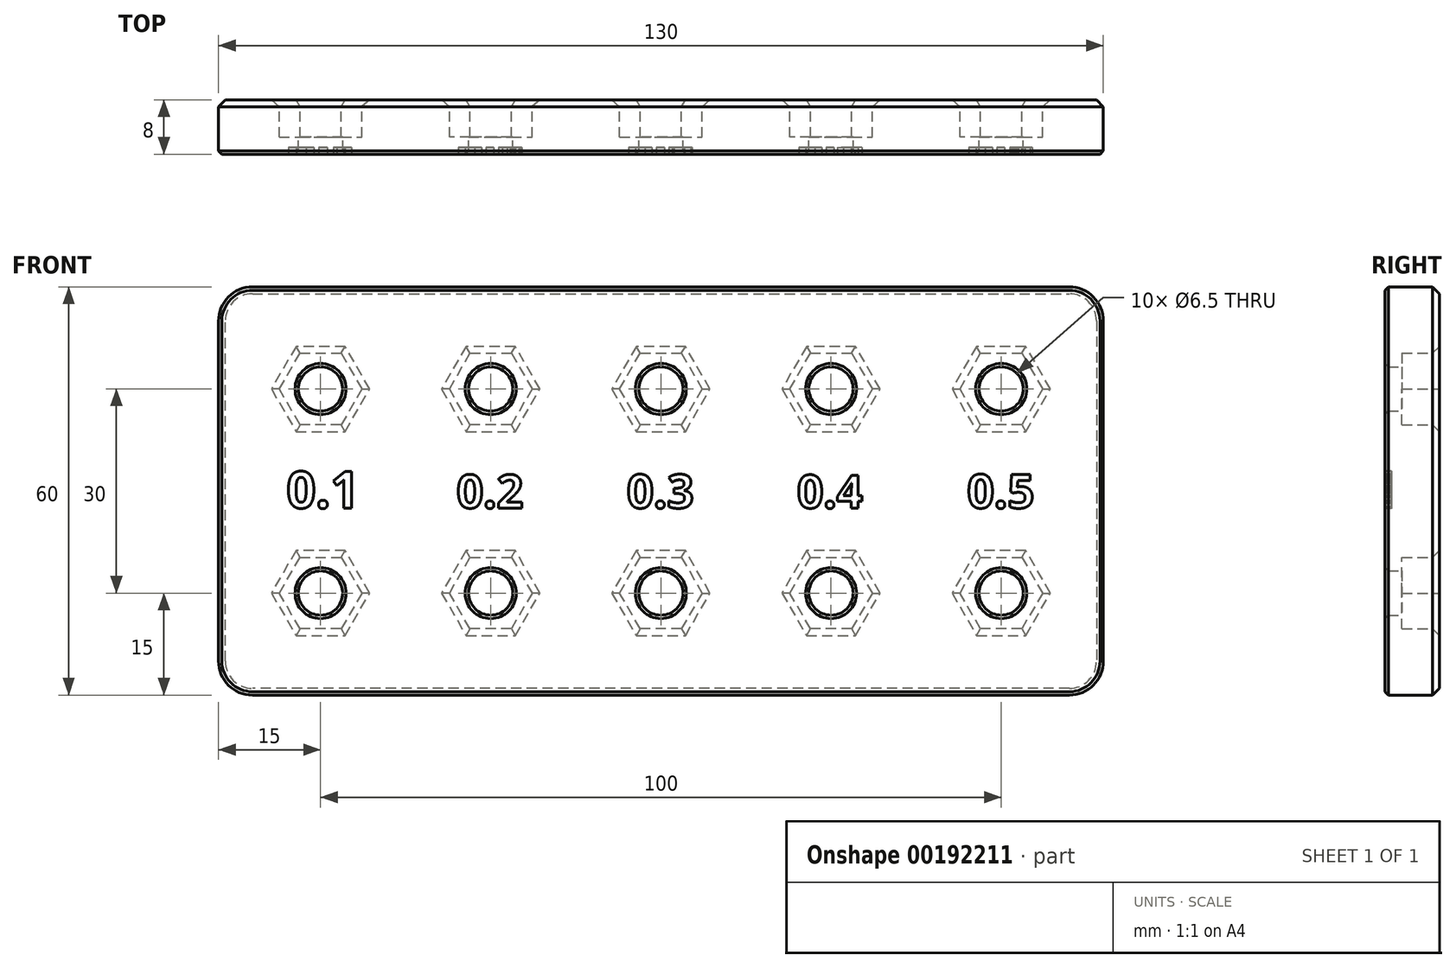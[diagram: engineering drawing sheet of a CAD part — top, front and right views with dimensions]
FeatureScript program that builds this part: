
annotation { "Feature Type Name" : "Feature", "Feature Type Description" : "" }
export const myFeature = defineFeature(function(context is Context, id is Id, definition is map)
    precondition{}
    {
        {
            var Q0;
            Q0=qCreatedBy(makeId("Front.planeOp"),FACE);
            var sketch = newSketch(context, id + "F0", { "sketchPlane" : qUnion([Q0])});
            skLineSegment(sketch, "E0.bottom", {"start": v(5, 0) * mm, "end": v(125, 0) * mm});
            skLineSegment(sketch, "E0.top", {"start": v(5, 60) * mm, "end": v(125, 60) * mm});
            skLineSegment(sketch, "E0.left", {"start": v(0, 5) * mm, "end": v(0, 55) * mm});
            skLineSegment(sketch, "E0.right", {"start": v(130, 5) * mm, "end": v(130, 55) * mm});
            skPoint(sketch, "E1.visualSharp", {"position": v(0, 60) * mm});
            skArc(sketch, "E1.filletArc", {"start": v(5, 60) * mm, "mid": v(1.46, 58.54) * mm, "end": v(0, 55) * mm});
            skPoint(sketch, "E2.visualSharp", {"position": v(130, 60) * mm});
            skArc(sketch, "E2.filletArc", {"start": v(130, 55) * mm, "mid": v(128.54, 58.54) * mm, "end": v(125, 60) * mm});
            skPoint(sketch, "E3.visualSharp", {"position": v(130, 0) * mm});
            skArc(sketch, "E3.filletArc", {"start": v(125, 0) * mm, "mid": v(128.54, 1.46) * mm, "end": v(130, 5) * mm});
            skPoint(sketch, "E4.visualSharp", {"position": v(0, 0) * mm});
            skArc(sketch, "E4.filletArc", {"start": v(0, 5) * mm, "mid": v(1.46, 1.46) * mm, "end": v(5, 0) * mm});
            skLineSegment(sketch, "E5", {"start": v(0, 45) * mm, "end": v(130, 45) * mm, "construction": true});
            skLineSegment(sketch, "E6", {"start": v(0, 15) * mm, "end": v(130, 15) * mm, "construction": true});
            skLineSegment(sketch, "E7", {"start": v(15, 60) * mm, "end": v(15, 0) * mm, "construction": true});
            skLineSegment(sketch, "E8.1.0.0", {"start": v(40, 60) * mm, "end": v(40, 0) * mm, "construction": true});
            skLineSegment(sketch, "E8.2.0.0", {"start": v(65, 60) * mm, "end": v(65, 0) * mm, "construction": true});
            skLineSegment(sketch, "E8.3.0.0", {"start": v(90, 60) * mm, "end": v(90, 0) * mm, "construction": true});
            skLineSegment(sketch, "E8.4.0.0", {"start": v(115, 60) * mm, "end": v(115, 0) * mm, "construction": true});
            skLineSegment(sketch, "E8.direction1", {"start": v(15, 0) * mm, "end": v(40, 0) * mm, "construction": true});
            skCircle(sketch, "E9", {"center": v(15, 45) * mm, "radius": 3.25 * mm});
            skCircle(sketch, "E10", {"center": v(40, 45) * mm, "radius": 3.25 * mm});
            skCircle(sketch, "E11", {"center": v(65, 45) * mm, "radius": 3.25 * mm});
            skCircle(sketch, "E12", {"center": v(90, 45) * mm, "radius": 3.25 * mm});
            skCircle(sketch, "E13", {"center": v(115, 45) * mm, "radius": 3.25 * mm});
            skCircle(sketch, "E14", {"center": v(15, 15) * mm, "radius": 3.25 * mm});
            skCircle(sketch, "E15", {"center": v(40, 15) * mm, "radius": 3.25 * mm});
            skCircle(sketch, "E16", {"center": v(65, 15) * mm, "radius": 3.25 * mm});
            skCircle(sketch, "E17", {"center": v(90, 15) * mm, "radius": 3.25 * mm});
            skCircle(sketch, "E18", {"center": v(115, 15) * mm, "radius": 3.25 * mm});
            skSolve(sketch);
        }
        {
            var Q0;
            Q0=makeQuery(id+"F0.imprint","IMPRINT",FACE,{"disambiguationData":[TD([[makeQuery(id+"F0.imprint","IMPRINT",EDGE,{"derivedFrom":sQuery(id+"F0.wireOp",EDGE,"E0.bottom")}),1.0]])]});
            extrude(context, id + "F1", {"entities" : qUnion([Q0]), "depth" : 8 * mm});
        }
        {
            var Q0;
            Q0=makeQuery(id+"F1.opExtrude","CAP_FACE",FACE,{"disambiguationData":[OSD([sQuery(id+"F0.wireOp",EDGE,"E0.bottom"),sQuery(id+"F0.wireOp",EDGE,"E0.top"),sQuery(id+"F0.wireOp",EDGE,"E0.left"),sQuery(id+"F0.wireOp",EDGE,"E0.right"),sQuery(id+"F0.wireOp",EDGE,"E1.filletArc"),sQuery(id+"F0.wireOp",EDGE,"E2.filletArc"),sQuery(id+"F0.wireOp",EDGE,"E3.filletArc"),sQuery(id+"F0.wireOp",EDGE,"E4.filletArc"),sQuery(id+"F0.wireOp",EDGE,"E9"),sQuery(id+"F0.wireOp",EDGE,"E10"),sQuery(id+"F0.wireOp",EDGE,"E11"),sQuery(id+"F0.wireOp",EDGE,"E12"),sQuery(id+"F0.wireOp",EDGE,"E13"),sQuery(id+"F0.wireOp",EDGE,"E14"),sQuery(id+"F0.wireOp",EDGE,"E15"),sQuery(id+"F0.wireOp",EDGE,"E16"),sQuery(id+"F0.wireOp",EDGE,"E17"),sQuery(id+"F0.wireOp",EDGE,"E18")])],"isStart":true});
            var sketch = newSketch(context, id + "F2", { "sketchPlane" : qUnion([Q0])});
            skCircle(sketch, "E19.cCircle", {"center": v(-115, 45) * mm, "radius": 5.25 * mm, "construction": true});
            skLineSegment(sketch, "E19.0", {"start": v(-108.94, 45) * mm, "end": v(-111.97, 39.75) * mm});
            skLineSegment(sketch, "E19.1", {"start": v(-111.97, 39.75) * mm, "end": v(-118.03, 39.75) * mm});
            skLineSegment(sketch, "E19.2", {"start": v(-118.03, 39.75) * mm, "end": v(-121.06, 45) * mm});
            skLineSegment(sketch, "E19.3", {"start": v(-121.06, 45) * mm, "end": v(-118.03, 50.25) * mm});
            skLineSegment(sketch, "E19.4", {"start": v(-118.03, 50.25) * mm, "end": v(-111.97, 50.25) * mm});
            skLineSegment(sketch, "E19.5", {"start": v(-111.97, 50.25) * mm, "end": v(-108.94, 45) * mm});
            skPoint(sketch, "E19.0.midPoint", {"position": v(-110.45, 42.37) * mm});
            skLineSegment(sketch, "E20", {"start": v(-130, 30) * mm, "end": v(0, 30) * mm, "construction": true});
            skPoint(sketch, "E21.1.0.0", {"position": v(-85.45, 42.37) * mm});
            skLineSegment(sketch, "E21.1.0.1", {"start": v(-93.03, 50.25) * mm, "end": v(-86.97, 50.25) * mm});
            skCircle(sketch, "E21.1.0.2", {"center": v(-90, 45) * mm, "radius": 5.25 * mm, "construction": true});
            skLineSegment(sketch, "E21.1.0.3", {"start": v(-83.94, 45) * mm, "end": v(-86.97, 39.75) * mm});
            skLineSegment(sketch, "E21.1.0.4", {"start": v(-86.97, 39.75) * mm, "end": v(-93.03, 39.75) * mm});
            skLineSegment(sketch, "E21.1.0.5", {"start": v(-96.06, 45) * mm, "end": v(-93.03, 50.25) * mm});
            skLineSegment(sketch, "E21.1.0.6", {"start": v(-93.03, 39.75) * mm, "end": v(-96.06, 45) * mm});
            skLineSegment(sketch, "E21.1.0.7", {"start": v(-86.97, 50.25) * mm, "end": v(-83.94, 45) * mm});
            skPoint(sketch, "E21.2.0.0", {"position": v(-60.45, 42.37) * mm});
            skLineSegment(sketch, "E21.2.0.1", {"start": v(-68.03, 50.25) * mm, "end": v(-61.97, 50.25) * mm});
            skCircle(sketch, "E21.2.0.2", {"center": v(-65, 45) * mm, "radius": 5.25 * mm, "construction": true});
            skLineSegment(sketch, "E21.2.0.3", {"start": v(-58.94, 45) * mm, "end": v(-61.97, 39.75) * mm});
            skLineSegment(sketch, "E21.2.0.4", {"start": v(-61.97, 39.75) * mm, "end": v(-68.03, 39.75) * mm});
            skLineSegment(sketch, "E21.2.0.5", {"start": v(-71.06, 45) * mm, "end": v(-68.03, 50.25) * mm});
            skLineSegment(sketch, "E21.2.0.6", {"start": v(-68.03, 39.75) * mm, "end": v(-71.06, 45) * mm});
            skLineSegment(sketch, "E21.2.0.7", {"start": v(-61.97, 50.25) * mm, "end": v(-58.94, 45) * mm});
            skPoint(sketch, "E21.3.0.0", {"position": v(-35.45, 42.37) * mm});
            skLineSegment(sketch, "E21.3.0.1", {"start": v(-43.03, 50.25) * mm, "end": v(-36.97, 50.25) * mm});
            skCircle(sketch, "E21.3.0.2", {"center": v(-40, 45) * mm, "radius": 5.25 * mm, "construction": true});
            skLineSegment(sketch, "E21.3.0.3", {"start": v(-33.94, 45) * mm, "end": v(-36.97, 39.75) * mm});
            skLineSegment(sketch, "E21.3.0.4", {"start": v(-36.97, 39.75) * mm, "end": v(-43.03, 39.75) * mm});
            skLineSegment(sketch, "E21.3.0.5", {"start": v(-46.06, 45) * mm, "end": v(-43.03, 50.25) * mm});
            skLineSegment(sketch, "E21.3.0.6", {"start": v(-43.03, 39.75) * mm, "end": v(-46.06, 45) * mm});
            skLineSegment(sketch, "E21.3.0.7", {"start": v(-36.97, 50.25) * mm, "end": v(-33.94, 45) * mm});
            skPoint(sketch, "E21.4.0.0", {"position": v(-10.45, 42.37) * mm});
            skLineSegment(sketch, "E21.4.0.1", {"start": v(-18.03, 50.25) * mm, "end": v(-11.97, 50.25) * mm});
            skCircle(sketch, "E21.4.0.2", {"center": v(-15, 45) * mm, "radius": 5.25 * mm, "construction": true});
            skLineSegment(sketch, "E21.4.0.3", {"start": v(-8.94, 45) * mm, "end": v(-11.97, 39.75) * mm});
            skLineSegment(sketch, "E21.4.0.4", {"start": v(-11.97, 39.75) * mm, "end": v(-18.03, 39.75) * mm});
            skLineSegment(sketch, "E21.4.0.5", {"start": v(-21.06, 45) * mm, "end": v(-18.03, 50.25) * mm});
            skLineSegment(sketch, "E21.4.0.6", {"start": v(-18.03, 39.75) * mm, "end": v(-21.06, 45) * mm});
            skLineSegment(sketch, "E21.4.0.7", {"start": v(-11.97, 50.25) * mm, "end": v(-8.94, 45) * mm});
            skLineSegment(sketch, "E21.direction1", {"start": v(-118.03, 39.75) * mm, "end": v(-93.03, 39.75) * mm, "construction": true});
            skLineSegment(sketch, "E22.MirrorCS", {"start": v(-43.03, 20.25) * mm, "end": v(-46.06, 15) * mm});
            skLineSegment(sketch, "E23.MirrorCS", {"start": v(-18.03, 9.75) * mm, "end": v(-11.97, 9.75) * mm});
            skLineSegment(sketch, "E24.MirrorCS", {"start": v(-68.03, 20.25) * mm, "end": v(-71.06, 15) * mm});
            skLineSegment(sketch, "E25.MirrorCS", {"start": v(-46.06, 15) * mm, "end": v(-43.03, 9.75) * mm});
            skLineSegment(sketch, "E26.MirrorCS", {"start": v(-11.97, 9.75) * mm, "end": v(-8.94, 15) * mm});
            skLineSegment(sketch, "E27.MirrorCS", {"start": v(-36.97, 9.75) * mm, "end": v(-33.94, 15) * mm});
            skLineSegment(sketch, "E28.MirrorCS", {"start": v(-71.06, 15) * mm, "end": v(-68.03, 9.75) * mm});
            skLineSegment(sketch, "E29.MirrorCS", {"start": v(-61.97, 9.75) * mm, "end": v(-58.94, 15) * mm});
            skLineSegment(sketch, "E30.MirrorCS", {"start": v(-8.94, 15) * mm, "end": v(-11.97, 20.25) * mm});
            skLineSegment(sketch, "E31.MirrorCS", {"start": v(-43.03, 9.75) * mm, "end": v(-36.97, 9.75) * mm});
            skLineSegment(sketch, "E32.MirrorCS", {"start": v(-61.97, 20.25) * mm, "end": v(-68.03, 20.25) * mm});
            skLineSegment(sketch, "E33.MirrorCS", {"start": v(-18.03, 20.25) * mm, "end": v(-21.06, 15) * mm});
            skLineSegment(sketch, "E34.MirrorCS", {"start": v(-96.06, 15) * mm, "end": v(-93.03, 9.75) * mm});
            skLineSegment(sketch, "E35.MirrorCS", {"start": v(-36.97, 20.25) * mm, "end": v(-43.03, 20.25) * mm});
            skLineSegment(sketch, "E36.MirrorCS", {"start": v(-86.97, 20.25) * mm, "end": v(-93.03, 20.25) * mm});
            skLineSegment(sketch, "E37.MirrorCS", {"start": v(-83.94, 15) * mm, "end": v(-86.97, 20.25) * mm});
            skLineSegment(sketch, "E38.MirrorCS", {"start": v(-93.03, 9.75) * mm, "end": v(-86.97, 9.75) * mm});
            skLineSegment(sketch, "E39.MirrorCS", {"start": v(-111.97, 9.75) * mm, "end": v(-108.94, 15) * mm});
            skLineSegment(sketch, "E40.MirrorCS", {"start": v(-118.03, 9.75) * mm, "end": v(-111.97, 9.75) * mm});
            skLineSegment(sketch, "E41.MirrorCS", {"start": v(-121.06, 15) * mm, "end": v(-118.03, 9.75) * mm});
            skLineSegment(sketch, "E42.MirrorCS", {"start": v(-118.03, 20.25) * mm, "end": v(-121.06, 15) * mm});
            skLineSegment(sketch, "E43.MirrorCS", {"start": v(-111.97, 20.25) * mm, "end": v(-118.03, 20.25) * mm});
            skLineSegment(sketch, "E44.MirrorCS", {"start": v(-58.94, 15) * mm, "end": v(-61.97, 20.25) * mm});
            skLineSegment(sketch, "E45.MirrorCS", {"start": v(-108.94, 15) * mm, "end": v(-111.97, 20.25) * mm});
            skLineSegment(sketch, "E46.MirrorCS", {"start": v(-21.06, 15) * mm, "end": v(-18.03, 9.75) * mm});
            skLineSegment(sketch, "E47.MirrorCS", {"start": v(-86.97, 9.75) * mm, "end": v(-83.94, 15) * mm});
            skLineSegment(sketch, "E48.MirrorCS", {"start": v(-11.97, 20.25) * mm, "end": v(-18.03, 20.25) * mm});
            skLineSegment(sketch, "E49.MirrorCS", {"start": v(-93.03, 20.25) * mm, "end": v(-96.06, 15) * mm});
            skLineSegment(sketch, "E50.MirrorCS", {"start": v(-33.94, 15) * mm, "end": v(-36.97, 20.25) * mm});
            skLineSegment(sketch, "E51.MirrorCS", {"start": v(-68.03, 9.75) * mm, "end": v(-61.97, 9.75) * mm});
            skLineSegment(sketch, "E52.MirrorCS", {"start": v(-118.03, 20.25) * mm, "end": v(-93.03, 20.25) * mm, "construction": true});
            skCircle(sketch, "E53.MirrorC", {"center": v(-15, 15) * mm, "radius": 5.25 * mm, "construction": true});
            skPoint(sketch, "E54.MirrorP", {"position": v(-60.45, 17.63) * mm});
            skPoint(sketch, "E55.MirrorP", {"position": v(-35.45, 17.63) * mm});
            skCircle(sketch, "E56.MirrorC", {"center": v(-40, 15) * mm, "radius": 5.25 * mm, "construction": true});
            skCircle(sketch, "E57.MirrorC", {"center": v(-90, 15) * mm, "radius": 5.25 * mm, "construction": true});
            skCircle(sketch, "E58.MirrorC", {"center": v(-115, 15) * mm, "radius": 5.25 * mm, "construction": true});
            skPoint(sketch, "E59.MirrorP", {"position": v(-110.45, 17.63) * mm});
            skCircle(sketch, "E60.MirrorC", {"center": v(-65, 15) * mm, "radius": 5.25 * mm, "construction": true});
            skPoint(sketch, "E61.MirrorP", {"position": v(-10.45, 17.63) * mm});
            skPoint(sketch, "E62.MirrorP", {"position": v(-85.45, 17.63) * mm});
            skSolve(sketch);
        }
        {
            var Q0;
            Q0 = qSketchRegion(id + "F2", true);
            extrude(context, id + "F3", {"entities" : qUnion([Q0]), "operationType" : NewBodyOperationType.REMOVE, "oppositeDirection" : true, "depth" : 5.5 * mm});
        }
        {
            var Q0;
            Q0=makeQuery(id+"F1.opExtrude","CAP_FACE",FACE,{"disambiguationData":[OSD([sQuery(id+"F0.wireOp",EDGE,"E0.bottom"),sQuery(id+"F0.wireOp",EDGE,"E0.top"),sQuery(id+"F0.wireOp",EDGE,"E0.left"),sQuery(id+"F0.wireOp",EDGE,"E0.right"),sQuery(id+"F0.wireOp",EDGE,"E1.filletArc"),sQuery(id+"F0.wireOp",EDGE,"E2.filletArc"),sQuery(id+"F0.wireOp",EDGE,"E3.filletArc"),sQuery(id+"F0.wireOp",EDGE,"E4.filletArc"),sQuery(id+"F0.wireOp",EDGE,"E9"),sQuery(id+"F0.wireOp",EDGE,"E10"),sQuery(id+"F0.wireOp",EDGE,"E11"),sQuery(id+"F0.wireOp",EDGE,"E12"),sQuery(id+"F0.wireOp",EDGE,"E13"),sQuery(id+"F0.wireOp",EDGE,"E14"),sQuery(id+"F0.wireOp",EDGE,"E15"),sQuery(id+"F0.wireOp",EDGE,"E16"),sQuery(id+"F0.wireOp",EDGE,"E17"),sQuery(id+"F0.wireOp",EDGE,"E18")])],"isStart":false});
            var sketch = newSketch(context, id + "F4", { "sketchPlane" : qUnion([Q0])});
            skText(sketch, "E63", { "text": "0.1", "fontName": "OpenSans-Bold.ttf"});
            skLineSegment(sketch, "E64", {"start": v(0, 27.5) * mm, "end": v(130, 27.5) * mm, "construction": true});
            skLineSegment(sketch, "E65", {"start": v(15, 45) * mm, "end": v(15, 15) * mm, "construction": true});
            skLineSegment(sketch, "E66.1.0.0", {"start": v(40, 45) * mm, "end": v(40, 15) * mm, "construction": true});
            skLineSegment(sketch, "E66.2.0.0", {"start": v(65, 45) * mm, "end": v(65, 15) * mm, "construction": true});
            skLineSegment(sketch, "E66.3.0.0", {"start": v(90, 45) * mm, "end": v(90, 15) * mm, "construction": true});
            skLineSegment(sketch, "E66.4.0.0", {"start": v(115, 45) * mm, "end": v(115, 15) * mm, "construction": true});
            skLineSegment(sketch, "E66.direction1", {"start": v(15, 15) * mm, "end": v(40, 15) * mm, "construction": true});
            skText(sketch, "E67", { "text": "0.2\n", "fontName": "OpenSans-Bold.ttf"});
            skText(sketch, "E68", { "text": "0.3\n", "fontName": "OpenSans-Bold.ttf"});
            skPoint(sketch, "E68.firstSnap0", {"position": v(65, 30) * mm});
            skText(sketch, "E69", { "text": "0.4\n", "fontName": "OpenSans-Bold.ttf"});
            skText(sketch, "E70", { "text": "0.5", "fontName": "OpenSans-Bold.ttf"});
            const initialGuessF4  = {"E63": [0.01, 0.0275, 1, 0, 0.0054], "E67": [0.035, 0.0275, 1, 0, 0.00493], "E68": [0.06, 0.0275, 1, 0, 0.00496], "E69": [0.085, 0.0275, 1, 0, 0.00488], "E70": [0.11, 0.0275, 1, 0, 0.00498]};
            skSetInitialGuess(sketch, initialGuessF4);
            skSolve(sketch);
        }
        {
            var Q0;
            Q0 = qSketchRegion(id + "F4", true);
            extrude(context, id + "F5", {"entities" : qUnion([Q0]), "operationType" : NewBodyOperationType.REMOVE, "oppositeDirection" : true, "depth" : 1 * mm});
        }
        {
            var Q0;
            Q0=makeQuery(id+"F1.opExtrude","CAP_FACE",FACE,{"disambiguationData":[OSD([sQuery(id+"F0.wireOp",EDGE,"E0.bottom"),sQuery(id+"F0.wireOp",EDGE,"E0.top"),sQuery(id+"F0.wireOp",EDGE,"E0.left"),sQuery(id+"F0.wireOp",EDGE,"E0.right"),sQuery(id+"F0.wireOp",EDGE,"E1.filletArc"),sQuery(id+"F0.wireOp",EDGE,"E2.filletArc"),sQuery(id+"F0.wireOp",EDGE,"E3.filletArc"),sQuery(id+"F0.wireOp",EDGE,"E4.filletArc"),sQuery(id+"F0.wireOp",EDGE,"E9"),sQuery(id+"F0.wireOp",EDGE,"E10"),sQuery(id+"F0.wireOp",EDGE,"E11"),sQuery(id+"F0.wireOp",EDGE,"E12"),sQuery(id+"F0.wireOp",EDGE,"E13"),sQuery(id+"F0.wireOp",EDGE,"E14"),sQuery(id+"F0.wireOp",EDGE,"E15"),sQuery(id+"F0.wireOp",EDGE,"E16"),sQuery(id+"F0.wireOp",EDGE,"E17"),sQuery(id+"F0.wireOp",EDGE,"E18")])],"isStart":true});
            chamfer(context, id + "F6", {"entities" : qUnion([Q0]), "width" : 1 * mm, "tangentPropagation" : true});
        }
        {
            var Q0;
            Q0=makeQuery(id+"F1.opExtrude","CAP_EDGE",EDGE,{"disambiguationData":[OSD([sQuery(id+"F0.wireOp",EDGE,"E0.left")])],"isStart":false});
            var Q1;
            Q1=makeQuery(id+"F1.opExtrude","CAP_EDGE",EDGE,{"disambiguationData":[OSD([sQuery(id+"F0.wireOp",EDGE,"E1.filletArc")])],"isStart":false});
            var Q2;
            Q2=makeQuery(id+"F1.opExtrude","CAP_EDGE",EDGE,{"disambiguationData":[OSD([sQuery(id+"F0.wireOp",EDGE,"E9")])],"isStart":false});
            var Q3;
            Q3=makeQuery(id+"F1.opExtrude","CAP_EDGE",EDGE,{"disambiguationData":[OSD([sQuery(id+"F0.wireOp",EDGE,"E10")])],"isStart":false});
            var Q4;
            Q4=makeQuery(id+"F1.opExtrude","CAP_EDGE",EDGE,{"disambiguationData":[OSD([sQuery(id+"F0.wireOp",EDGE,"E11")])],"isStart":false});
            var Q5;
            Q5=makeQuery(id+"F1.opExtrude","CAP_EDGE",EDGE,{"disambiguationData":[OSD([sQuery(id+"F0.wireOp",EDGE,"E12")])],"isStart":false});
            var Q6;
            Q6=makeQuery(id+"F1.opExtrude","CAP_EDGE",EDGE,{"disambiguationData":[OSD([sQuery(id+"F0.wireOp",EDGE,"E13")])],"isStart":false});
            var Q7;
            Q7=makeQuery(id+"F1.opExtrude","CAP_EDGE",EDGE,{"disambiguationData":[OSD([sQuery(id+"F0.wireOp",EDGE,"E14")])],"isStart":false});
            var Q8;
            Q8=makeQuery(id+"F1.opExtrude","CAP_EDGE",EDGE,{"disambiguationData":[OSD([sQuery(id+"F0.wireOp",EDGE,"E15")])],"isStart":false});
            var Q9;
            Q9=makeQuery(id+"F1.opExtrude","CAP_EDGE",EDGE,{"disambiguationData":[OSD([sQuery(id+"F0.wireOp",EDGE,"E16")])],"isStart":false});
            var Q10;
            Q10=makeQuery(id+"F1.opExtrude","CAP_EDGE",EDGE,{"disambiguationData":[OSD([sQuery(id+"F0.wireOp",EDGE,"E17")])],"isStart":false});
            var Q11;
            Q11=makeQuery(id+"F1.opExtrude","CAP_EDGE",EDGE,{"disambiguationData":[OSD([sQuery(id+"F0.wireOp",EDGE,"E18")])],"isStart":false});
            chamfer(context, id + "F7", {"entities" : qUnion([Q0, Q1, Q2, Q3, Q4, Q5, Q6, Q7, Q8, Q9, Q10, Q11]), "width" : 0.5 * mm, "tangentPropagation" : true});
        }
    });
